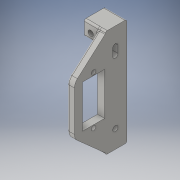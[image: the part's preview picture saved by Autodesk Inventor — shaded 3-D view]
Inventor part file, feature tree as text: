
AUTODESK INVENTOR PART (.ipt)
format: ipt  version: 2016 (Build 200138000, 138)  size: 366,592 bytes
history: native  units: in
note: dims shown in document units (in); Inventor stores cm internally (conversion verified against a paired STEP export)
features: projected_geometry x11, extrude x9, sketch x9, fillet x2, other x1
ambient origin geometry x8: Origin, YZ Plane, XZ Plane, XY Plane, X Axis, Y Axis, Z Axis, Center Point
bodies: Solid1 (feature_tree)
feature tree (32):
  extrude  "Extrusion2"  Depth=0.9449in
  extrude  "Extrusion3"  Depth=0.3937in TaperAngle=0.0deg
  extrude  "Extrusion4"  Depth=0.0079in
  extrude  "Extrusion5"  Depth=0.1173in
  extrude  "Extrusion7"  Depth=0.2205in
  extrude  "Extrusion6"  Depth=2.0472in
  extrude  "Extrusion8"  Depth=39.3701in TaperAngle=0.0deg
  extrude  "Extrusion9"  Depth=39.3701in TaperAngle=0.0deg
  extrude  "Extrusion10"  Depth=0.0394in
  fillet  "Fillet1"  Radius=0.0591in
  fillet  "Fillet2"  Radius=0.0591in
  sketch  "Sketch2"  dims[d3=0.4921in d4=0.9449in]
  projected_geometry  "Projected Loop2"
  sketch  "Sketch3"  dims[d5=0.3937in d6=0.0in d7=0.0787in d8=0.0in]
  projected_geometry  "Projected Loop3"
  projected_geometry  "Projected Loop4"
  sketch  "Sketch4"  dims[d9=0.4722in d10=0.0in d11=0.0079in]
  sketch  "Sketch5"  dims[d12=0.4722in d13=0.0in d14=0.1173in]
  projected_geometry  "Projected Loop5"
  sketch  "Sketch6"  dims[d16=0.1969in d17=0.2205in]
  projected_geometry  "Projected Loop6"
  projected_geometry  "Projected Loop7"
  sketch  "Sketch7"  dims[d18=39.3701in d19=0.0in d20=2.0472in]
  projected_geometry  "Projected Loop8"
  sketch  "Sketch9"  dims[d21=0.2835in d22=39.3701in d23=0.0in]
  projected_geometry  "Projected Loop9"
  sketch  "Sketch10"  dims[d24=0.1575in d25=39.3701in d26=0.0in]
  projected_geometry  "Projected Loop10"
  sketch  "Sketch11"  dims[d31=0.2362in d32=0.1181in d33=0.0591in d34=0.0591in d35=0.0394in d36=0.0in d37=0.0787in d38=0.0394in d39=0.0787in d40=0.0394in d41=0.0in]
  projected_geometry  "Projected Loop11"
  projected_geometry  "Projected Loop12"
  other  "servoHolder"
